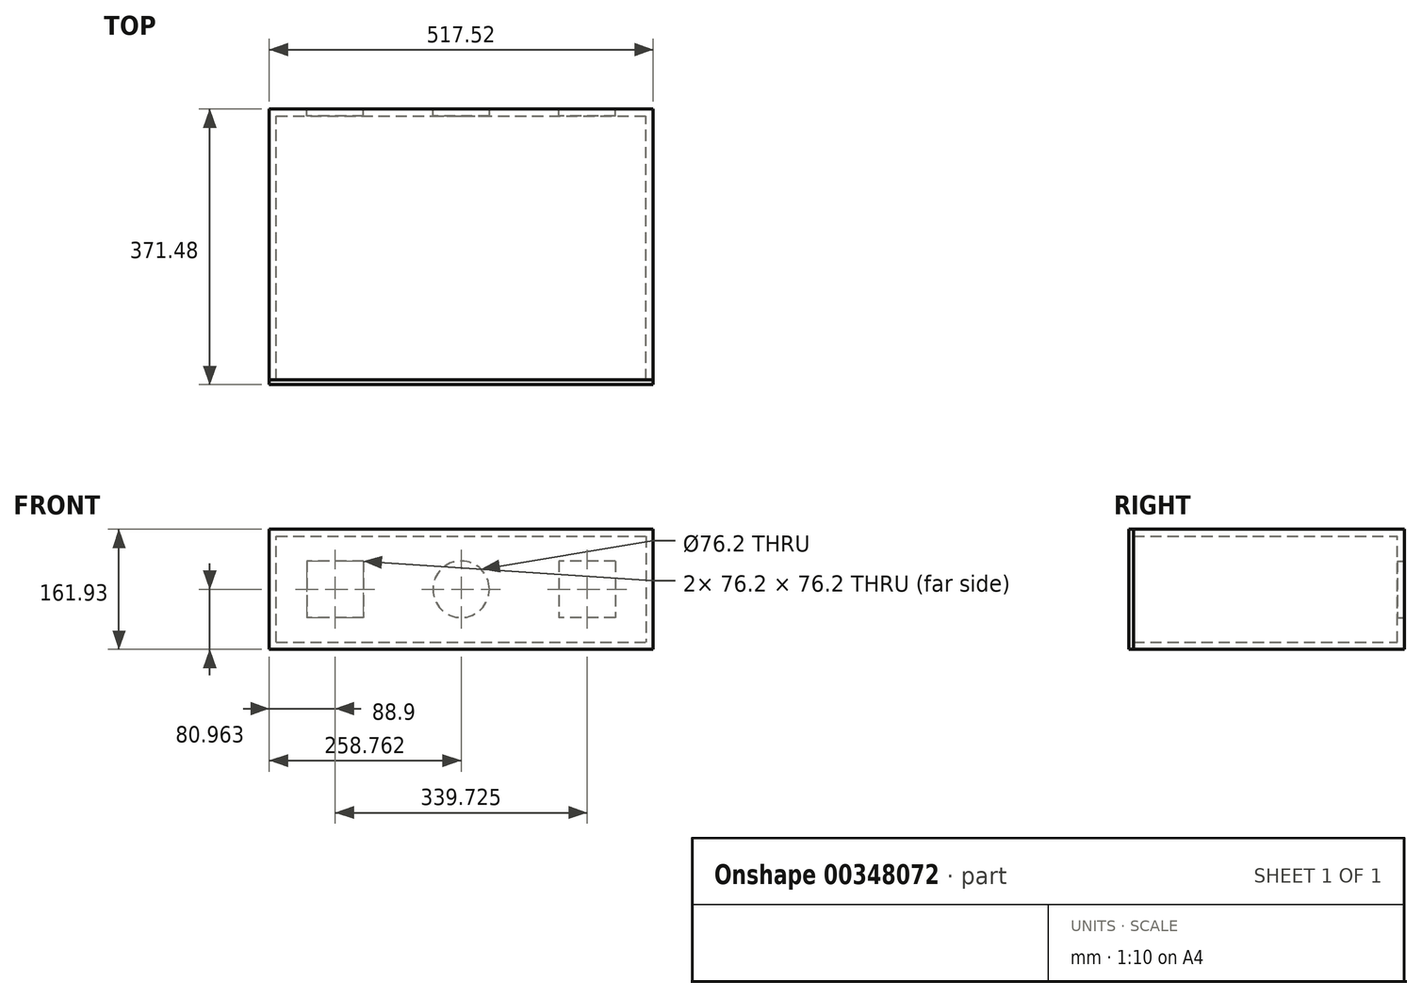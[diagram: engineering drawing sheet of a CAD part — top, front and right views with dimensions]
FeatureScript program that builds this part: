
annotation { "Feature Type Name" : "Feature", "Feature Type Description" : "" }
export const myFeature = defineFeature(function(context is Context, id is Id, definition is map)
    precondition{}
    {
        {
            var Q0;
            Q0=qCreatedBy(makeId("Top.planeOp"),FACE);
            var sketch = newSketch(context, id + "F0", { "sketchPlane" : qUnion([Q0])});
            skLineSegment(sketch, "E0.bottom", {"start": v(0, 0) * mm, "end": v(508, 0) * mm});
            skLineSegment(sketch, "E0.top", {"start": v(0, 355.6) * mm, "end": v(508, 355.6) * mm});
            skLineSegment(sketch, "E0.left", {"start": v(0, 0) * mm, "end": v(0, 355.6) * mm});
            skLineSegment(sketch, "E0.right", {"start": v(508, 0) * mm, "end": v(508, 355.6) * mm});
            skSolve(sketch);
        }
        {
            var Q0;
            Q0 = qSketchRegion(id + "F0", true);
            extrude(context, id + "F1", {"entities" : qUnion([Q0]), "depth" : 9.52 * mm});
        }
        {
            var Q0;
            Q0=makeQuery(id+"F1.opExtrude","SWEPT_FACE",FACE,{"disambiguationData":[OSD([sQuery(id+"F0.wireOp",EDGE,"E0.right")])]});
            var sketch = newSketch(context, id + "F2", { "sketchPlane" : qUnion([Q0])});
            skLineSegment(sketch, "E1.bottom", {"start": v(0, 0) * mm, "end": v(355.6, 0) * mm});
            skLineSegment(sketch, "E1.top", {"start": v(0, 152.4) * mm, "end": v(355.6, 152.4) * mm});
            skLineSegment(sketch, "E1.left", {"start": v(0, 0) * mm, "end": v(0, 152.4) * mm});
            skLineSegment(sketch, "E1.right", {"start": v(355.6, 0) * mm, "end": v(355.6, 152.4) * mm});
            skSolve(sketch);
        }
        {
            var Q0;
            Q0 = qSketchRegion(id + "F2", true);
            extrude(context, id + "F3", {"entities" : qUnion([Q0]), "operationType" : NewBodyOperationType.ADD, "depth" : 9.52 * mm});
        }
        {
            var Q0;
            Q0=qCreatedBy(makeId("Right.planeOp"),FACE);
            var sketch = newSketch(context, id + "F4", { "sketchPlane" : qUnion([Q0])});
            skLineSegment(sketch, "E2.bottom", {"start": v(0, 0) * mm, "end": v(355.6, 0) * mm});
            skLineSegment(sketch, "E2.top", {"start": v(0, 152.4) * mm, "end": v(355.6, 152.4) * mm});
            skLineSegment(sketch, "E2.left", {"start": v(0, 0) * mm, "end": v(0, 152.4) * mm});
            skLineSegment(sketch, "E2.right", {"start": v(355.6, 0) * mm, "end": v(355.6, 152.4) * mm});
            skSolve(sketch);
        }
        {
            var Q0;
            Q0 = qSketchRegion(id + "F4", true);
            extrude(context, id + "F5", {"entities" : qUnion([Q0]), "operationType" : NewBodyOperationType.ADD, "depth" : 9.52 * mm});
        }
        {
            var Q0;
            Q0=makeQuery(id+"F5.opExtrude","SWEPT_FACE",FACE,{"disambiguationData":[OSD([sQuery(id+"F4.wireOp",EDGE,"E2.top")])]});
            var sketch = newSketch(context, id + "F6", { "sketchPlane" : qUnion([Q0])});
            skLineSegment(sketch, "E3.bottom", {"start": v(0, 0) * mm, "end": v(517.52, 0) * mm});
            skLineSegment(sketch, "E3.top", {"start": v(0, 355.6) * mm, "end": v(517.52, 355.6) * mm});
            skLineSegment(sketch, "E3.left", {"start": v(0, 0) * mm, "end": v(0, 355.6) * mm});
            skLineSegment(sketch, "E3.right", {"start": v(517.52, 0) * mm, "end": v(517.52, 355.6) * mm});
            skSolve(sketch);
        }
        {
            var Q0;
            Q0 = qSketchRegion(id + "F6", true);
            extrude(context, id + "F7", {"entities" : qUnion([Q0]), "operationType" : NewBodyOperationType.ADD, "depth" : 9.52 * mm});
        }
        {
            var Q0;
            Q0=makeQuery(id+"F7.boolean.opBoolean","MERGE",FACE,{"derivedFrom":[makeQuery(id+"F5.boolean.opBoolean","MERGE",FACE,{"derivedFrom":[makeQuery(id+"F3.boolean.opBoolean","MERGE",FACE,{"derivedFrom":[makeQuery(id+"F1.opExtrude","SWEPT_FACE",FACE,{"disambiguationData":[OSD([sQuery(id+"F0.wireOp",EDGE,"E0.top")])]}),makeQuery(id+"F3.opExtrude","SWEPT_FACE",FACE,{"disambiguationData":[OSD([sQuery(id+"F2.wireOp",EDGE,"E1.right")])]})]}),makeQuery(id+"F5.opExtrude","SWEPT_FACE",FACE,{"disambiguationData":[OSD([sQuery(id+"F4.wireOp",EDGE,"E2.right")])]})]}),makeQuery(id+"F7.opExtrude","SWEPT_FACE",FACE,{"disambiguationData":[OSD([sQuery(id+"F6.wireOp",EDGE,"E3.top")])]})]});
            var sketch = newSketch(context, id + "F8", { "sketchPlane" : qUnion([Q0])});
            skLineSegment(sketch, "E4.bottom", {"start": v(-517.53, 0) * mm, "end": v(0, 0) * mm});
            skLineSegment(sketch, "E4.top", {"start": v(-517.53, 161.92) * mm, "end": v(0, 161.92) * mm});
            skLineSegment(sketch, "E4.left", {"start": v(-517.53, 0) * mm, "end": v(-517.53, 161.92) * mm});
            skLineSegment(sketch, "E4.right", {"start": v(0, 0) * mm, "end": v(0, 161.92) * mm});
            skSolve(sketch);
        }
        {
            var Q0;
            Q0 = qSketchRegion(id + "F8", true);
            extrude(context, id + "F9", {"entities" : qUnion([Q0]), "operationType" : NewBodyOperationType.ADD, "depth" : 9.52 * mm});
        }
        {
            var Q0;
            Q0=makeQuery(id+"F7.boolean.opBoolean","MERGE",FACE,{"derivedFrom":[makeQuery(id+"F5.boolean.opBoolean","MERGE",FACE,{"derivedFrom":[makeQuery(id+"F3.boolean.opBoolean","MERGE",FACE,{"derivedFrom":[makeQuery(id+"F1.opExtrude","SWEPT_FACE",FACE,{"disambiguationData":[OSD([sQuery(id+"F0.wireOp",EDGE,"E0.bottom")])]}),makeQuery(id+"F3.opExtrude","SWEPT_FACE",FACE,{"disambiguationData":[OSD([sQuery(id+"F2.wireOp",EDGE,"E1.left")])]})]}),makeQuery(id+"F5.opExtrude","SWEPT_FACE",FACE,{"disambiguationData":[OSD([sQuery(id+"F4.wireOp",EDGE,"E2.left")])]})]}),makeQuery(id+"F7.opExtrude","SWEPT_FACE",FACE,{"disambiguationData":[OSD([sQuery(id+"F6.wireOp",EDGE,"E3.bottom")])]})]});
            var sketch = newSketch(context, id + "F10", { "sketchPlane" : qUnion([Q0])});
            skLineSegment(sketch, "E5.bottom", {"start": v(0, 0) * mm, "end": v(517.52, 0) * mm});
            skLineSegment(sketch, "E5.top", {"start": v(0, 161.93) * mm, "end": v(517.52, 161.93) * mm});
            skLineSegment(sketch, "E5.left", {"start": v(0, 0) * mm, "end": v(0, 161.93) * mm});
            skLineSegment(sketch, "E5.right", {"start": v(517.52, 0) * mm, "end": v(517.52, 161.93) * mm});
            skSolve(sketch);
        }
        {
            var Q0;
            Q0 = qSketchRegion(id + "F10", true);
            extrude(context, id + "F11", {"entities" : qUnion([Q0]), "depth" : 6.35 * mm});
        }
        {
            var Q0;
            Q0=makeQuery(id+"F9.opExtrude","CAP_FACE",FACE,{"disambiguationData":[OSD([sQuery(id+"F8.wireOp",EDGE,"E4.bottom"),sQuery(id+"F8.wireOp",EDGE,"E4.top"),sQuery(id+"F8.wireOp",EDGE,"E4.left"),sQuery(id+"F8.wireOp",EDGE,"E4.right")])],"isStart":false});
            var sketch = newSketch(context, id + "F12", { "sketchPlane" : qUnion([Q0])});
            skLineSegment(sketch, "E6.bottom", {"start": v(-466.73, 119.06) * mm, "end": v(-390.53, 119.06) * mm});
            skLineSegment(sketch, "E6.top", {"start": v(-466.73, 42.86) * mm, "end": v(-390.53, 42.86) * mm});
            skLineSegment(sketch, "E6.left", {"start": v(-466.73, 119.06) * mm, "end": v(-466.73, 42.86) * mm});
            skLineSegment(sketch, "E6.right", {"start": v(-390.53, 119.06) * mm, "end": v(-390.53, 42.86) * mm});
            skLineSegment(sketch, "E7.bottom", {"start": v(-127, 119.06) * mm, "end": v(-50.8, 119.06) * mm});
            skLineSegment(sketch, "E7.top", {"start": v(-127, 42.86) * mm, "end": v(-50.8, 42.86) * mm});
            skLineSegment(sketch, "E7.left", {"start": v(-127, 119.06) * mm, "end": v(-127, 42.86) * mm});
            skLineSegment(sketch, "E7.right", {"start": v(-50.8, 119.06) * mm, "end": v(-50.8, 42.86) * mm});
            skCircle(sketch, "E8", {"center": v(-258.76, 80.96) * mm, "radius": 38.1 * mm});
            skSolve(sketch);
        }
        {
            var Q0;
            Q0 = qSketchRegion(id + "F12", true);
            extrude(context, id + "F13", {"entities" : qUnion([Q0]), "operationType" : NewBodyOperationType.REMOVE, "oppositeDirection" : true, "depth" : 25.4 * mm});
        }
    });
